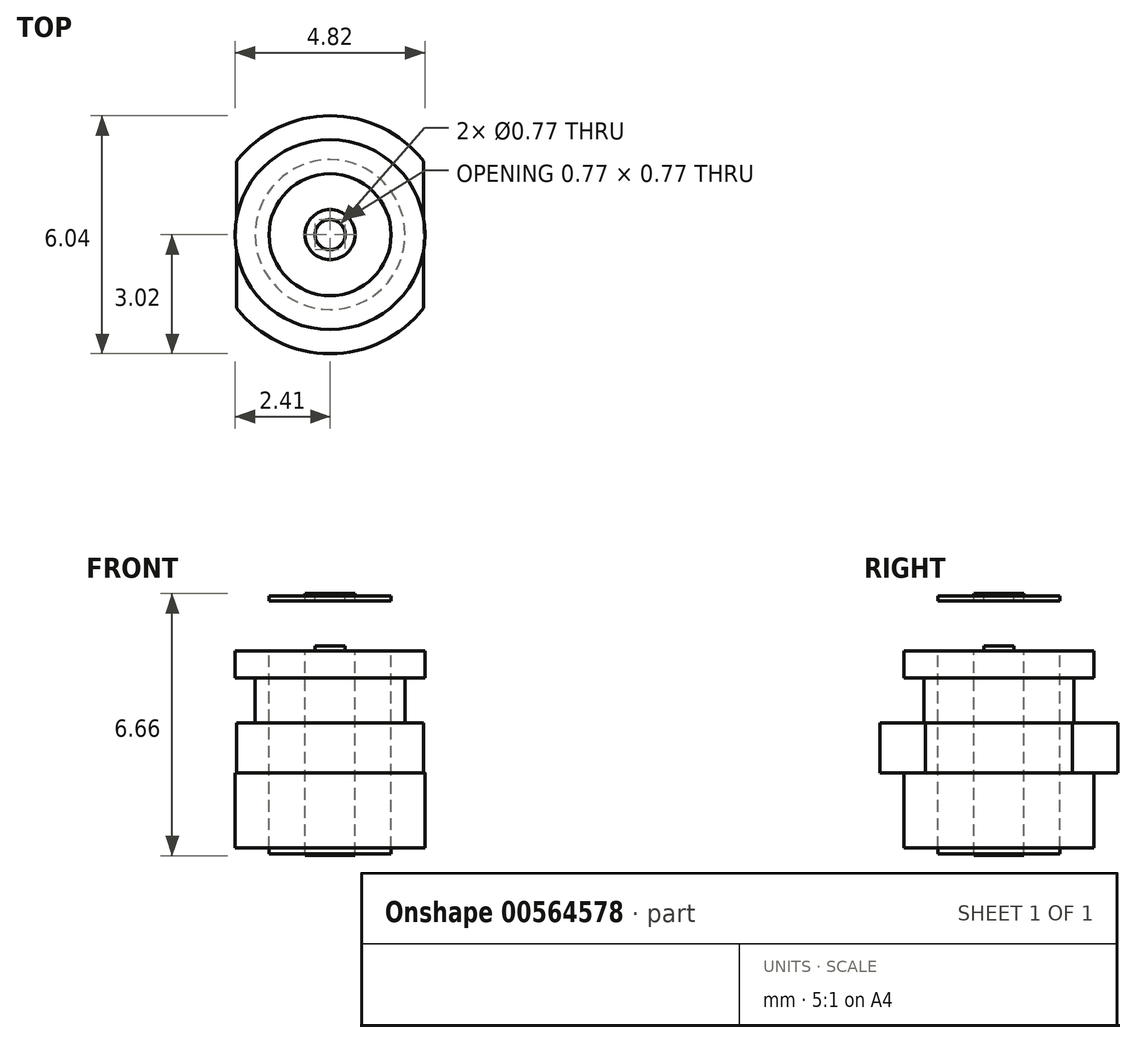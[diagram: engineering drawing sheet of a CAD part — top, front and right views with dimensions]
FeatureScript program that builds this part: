
annotation { "Feature Type Name" : "Feature", "Feature Type Description" : "" }
export const myFeature = defineFeature(function(context is Context, id is Id, definition is map)
    precondition{}
    {
        {
            var Q0;
            Q0=qCreatedBy(makeId("Top.planeOp"),FACE);
            var sketch = newSketch(context, id + "F0", { "sketchPlane" : qUnion([Q0])});
            skArc(sketch, "E0", {"start": v(2.37, 1.87) * mm, "mid": v(0, 3.02) * mm, "end": v(-2.37, 1.87) * mm});
            skLineSegment(sketch, "E1.left", {"start": v(2.37, -1.87) * mm, "end": v(2.37, 1.87) * mm});
            skLineSegment(sketch, "E1.right", {"start": v(-2.37, -1.87) * mm, "end": v(-2.37, 1.87) * mm});
            skArc(sketch, "E2.trimOffspring", {"start": v(-2.37, -1.87) * mm, "mid": v(0, -3.02) * mm, "end": v(2.37, -1.87) * mm});
            skPoint(sketch, "E1.top.end.orphan", {"position": v(-2.37, 5.75) * mm});
            skPoint(sketch, "E1.top.start.orphan", {"position": v(2.37, 5.75) * mm});
            skPoint(sketch, "E1.bottom.start.orphan", {"position": v(2.37, -5.75) * mm});
            skPoint(sketch, "E3.orphan", {"position": v(-2.37, -5.75) * mm});
            skSolve(sketch);
        }
        {
            var Q0;
            Q0=makeQuery(id+"F0.imprint","IMPRINT",FACE,{"disambiguationData":[TD([[makeQuery(id+"F0.imprint","IMPRINT",EDGE,{"derivedFrom":sQuery(id+"F0.wireOp",EDGE,"E0")}),1.0]])]});
            extrude(context, id + "F1", {"entities" : qUnion([Q0]), "depth" : 1.27 * mm, "offsetDistance" : 25.4 * mm});
        }
        {
            var Q0;
            Q0=makeQuery(id+"F1.opExtrude","CAP_FACE",FACE,{"disambiguationData":[OSD([sQuery(id+"F0.wireOp",EDGE,"E0"),sQuery(id+"F0.wireOp",EDGE,"E1.left"),sQuery(id+"F0.wireOp",EDGE,"E1.right"),sQuery(id+"F0.wireOp",EDGE,"E2.trimOffspring")])],"isStart":true});
            var sketch = newSketch(context, id + "F2", { "sketchPlane" : qUnion([Q0])});
            skCircle(sketch, "E4", {"center": v(0, 0) * mm, "radius": 2.41 * mm});
            skSolve(sketch);
        }
        {
            var Q0;
            Q0 = qSketchRegion(id + "F2", true);
            extrude(context, id + "F3", {"entities" : qUnion([Q0]), "operationType" : NewBodyOperationType.ADD, "depth" : 1.9 * mm, "offsetDistance" : 25.4 * mm});
        }
        {
            var Q0;
            Q0=makeQuery(id+"F1.opExtrude","CAP_FACE",FACE,{"disambiguationData":[OSD([sQuery(id+"F0.wireOp",EDGE,"E0"),sQuery(id+"F0.wireOp",EDGE,"E1.left"),sQuery(id+"F0.wireOp",EDGE,"E1.right"),sQuery(id+"F0.wireOp",EDGE,"E2.trimOffspring")])],"isStart":false});
            var sketch = newSketch(context, id + "F4", { "sketchPlane" : qUnion([Q0])});
            skCircle(sketch, "E5", {"center": v(0, 0) * mm, "radius": 1.9 * mm});
            skSolve(sketch);
        }
        {
            var Q0;
            Q0=makeQuery(id+"F4.imprint","IMPRINT",FACE,{"disambiguationData":[TD([[makeQuery(id+"F4.imprint","IMPRINT",EDGE,{"derivedFrom":sQuery(id+"F4.wireOp",EDGE,"E5")}),1.0]])]});
            extrude(context, id + "F5", {"entities" : qUnion([Q0]), "operationType" : NewBodyOperationType.ADD, "depth" : 1.14 * mm, "offsetDistance" : 25.4 * mm});
        }
        {
            var Q0;
            Q0=makeQuery(id+"F5.opExtrude","CAP_FACE",FACE,{"disambiguationData":[OSD([sQuery(id+"F4.wireOp",EDGE,"E5")])],"isStart":false});
            var sketch = newSketch(context, id + "F6", { "sketchPlane" : qUnion([Q0])});
            skCircle(sketch, "E6", {"center": v(0, 0) * mm, "radius": 2.41 * mm});
            skSolve(sketch);
        }
        {
            var Q0;
            Q0 = qSketchRegion(id + "F6", true);
            extrude(context, id + "F7", {"entities" : qUnion([Q0]), "operationType" : NewBodyOperationType.ADD, "depth" : 1.96 * mm, "offsetDistance" : 25.4 * mm});
        }
        {
            var Q0;
            Q0=makeQuery(id+"F7.opExtrude","CAP_FACE",FACE,{"disambiguationData":[OSD([sQuery(id+"F6.wireOp",EDGE,"E6")])],"isStart":false});
            var sketch = newSketch(context, id + "F8", { "sketchPlane" : qUnion([Q0])});
            skCircle(sketch, "E7", {"center": v(0, 0) * mm, "radius": 1.55 * mm});
            skSolve(sketch);
        }
        {
            var Q0;
            Q0=makeQuery(id+"F8.imprint","IMPRINT",FACE,{"disambiguationData":[TD([[makeQuery(id+"F8.imprint","IMPRINT",EDGE,{"derivedFrom":sQuery(id+"F8.wireOp",EDGE,"E7")}),1.0]])]});
            extrude(context, id + "F9", {"entities" : qUnion([Q0]), "oppositeDirection" : true, "depth" : 6.55 * mm, "offsetDistance" : 25.4 * mm});
        }
        {
            var Q0;
            Q0=makeQuery(id+"F9.opExtrude","SWEPT_BODY",BODY,{"disambiguationData":[OSD([sQuery(id+"F8.wireOp",EDGE,"E7")])]});
            transform(context, id + "F10", {"entities" : qUnion([Q0]), "transformType" : TransformType.TRANSLATION_3D, "dx" : 0 * mm, "dy" : 0 * mm, "dz" : 0.13 * mm, "makeCopy" : false});
        }
        {
            var Q0;
            Q0=makeQuery(id+"F9.opExtrude","CAP_FACE",FACE,{"disambiguationData":[OSD([sQuery(id+"F8.wireOp",EDGE,"E7")])],"isStart":true});
            var sketch = newSketch(context, id + "F11", { "sketchPlane" : qUnion([Q0])});
            skCircle(sketch, "E8", {"center": v(0, 0) * mm, "radius": 0.64 * mm});
            skSolve(sketch);
        }
        {
            var Q0;
            Q0 = qSketchRegion(id + "F11", true);
            extrude(context, id + "F12", {"entities" : qUnion([Q0]), "oppositeDirection" : true, "depth" : 6.65 * mm, "offsetDistance" : 25.4 * mm});
        }
        {
            var Q0;
            Q0=makeQuery(id+"F12.opExtrude","SWEPT_BODY",BODY,{"disambiguationData":[OSD([sQuery(id+"F11.wireOp",EDGE,"E8")])]});
            transform(context, id + "F13", {"entities" : qUnion([Q0]), "transformType" : TransformType.TRANSLATION_3D, "dx" : 0 * mm, "dy" : 0 * mm, "dz" : 0.06 * mm, "makeCopy" : false});
        }
        {
            var Q0;
            Q0=makeQuery(id+"F12.opExtrude","CAP_FACE",FACE,{"disambiguationData":[OSD([sQuery(id+"F11.wireOp",EDGE,"E8")])],"isStart":true});
            var sketch = newSketch(context, id + "F14", { "sketchPlane" : qUnion([Q0])});
            skCircle(sketch, "E9", {"center": v(0, 0) * mm, "radius": 0.38 * mm});
            skSolve(sketch);
        }
        {
            var Q0;
            Q0=makeQuery(id+"F14.imprint","IMPRINT",FACE,{"disambiguationData":[TD([[makeQuery(id+"F14.imprint","IMPRINT",EDGE,{"derivedFrom":sQuery(id+"F14.wireOp",EDGE,"E9")}),1.0]])]});
            extrude(context, id + "F15", {"entities" : qUnion([Q0]), "operationType" : NewBodyOperationType.REMOVE, "oppositeDirection" : true, "depth" : 1.27 * mm, "offsetDistance" : 25.4 * mm});
        }
        {
            var Q0;
            Q0=makeQuery(id+"F9.opExtrude","CAP_FACE",FACE,{"disambiguationData":[OSD([sQuery(id+"F8.wireOp",EDGE,"E7")])],"isStart":true});
            var sketch = newSketch(context, id + "F16", { "sketchPlane" : qUnion([Q0])});
            skCircle(sketch, "E10", {"center": v(0, 0) * mm, "radius": 0.38 * mm});
            skSolve(sketch);
        }
        {
            var Q0;
            Q0=makeQuery(id+"F16.imprint","IMPRINT",FACE,{"disambiguationData":[TD([[makeQuery(id+"F16.imprint","IMPRINT",EDGE,{"derivedFrom":sQuery(id+"F16.wireOp",EDGE,"E10")}),1.0]])]});
            extrude(context, id + "F17", {"entities" : qUnion([Q0]), "operationType" : NewBodyOperationType.REMOVE, "oppositeDirection" : true, "depth" : 1.27 * mm, "offsetDistance" : 25.4 * mm});
        }
        {
            var Q0;
            Q0=makeQuery(id+"F7.opExtrude","CAP_FACE",FACE,{"disambiguationData":[OSD([sQuery(id+"F6.wireOp",EDGE,"E6")])],"isStart":false});
            var sketch = newSketch(context, id + "F18", { "sketchPlane" : qUnion([Q0])});
            skCircle(sketch, "E11", {"center": v(0, 0) * mm, "radius": 0.38 * mm});
            skSolve(sketch);
        }
        {
            var Q0;
            Q0=makeQuery(id+"F18.imprint","IMPRINT",FACE,{"disambiguationData":[TD([[makeQuery(id+"F18.imprint","IMPRINT",EDGE,{"derivedFrom":sQuery(id+"F18.wireOp",EDGE,"E11")}),1.0]])]});
            extrude(context, id + "F19", {"entities" : qUnion([Q0]), "operationType" : NewBodyOperationType.REMOVE, "oppositeDirection" : true, "depth" : 1.27 * mm, "offsetDistance" : 25.4 * mm});
        }
    });
